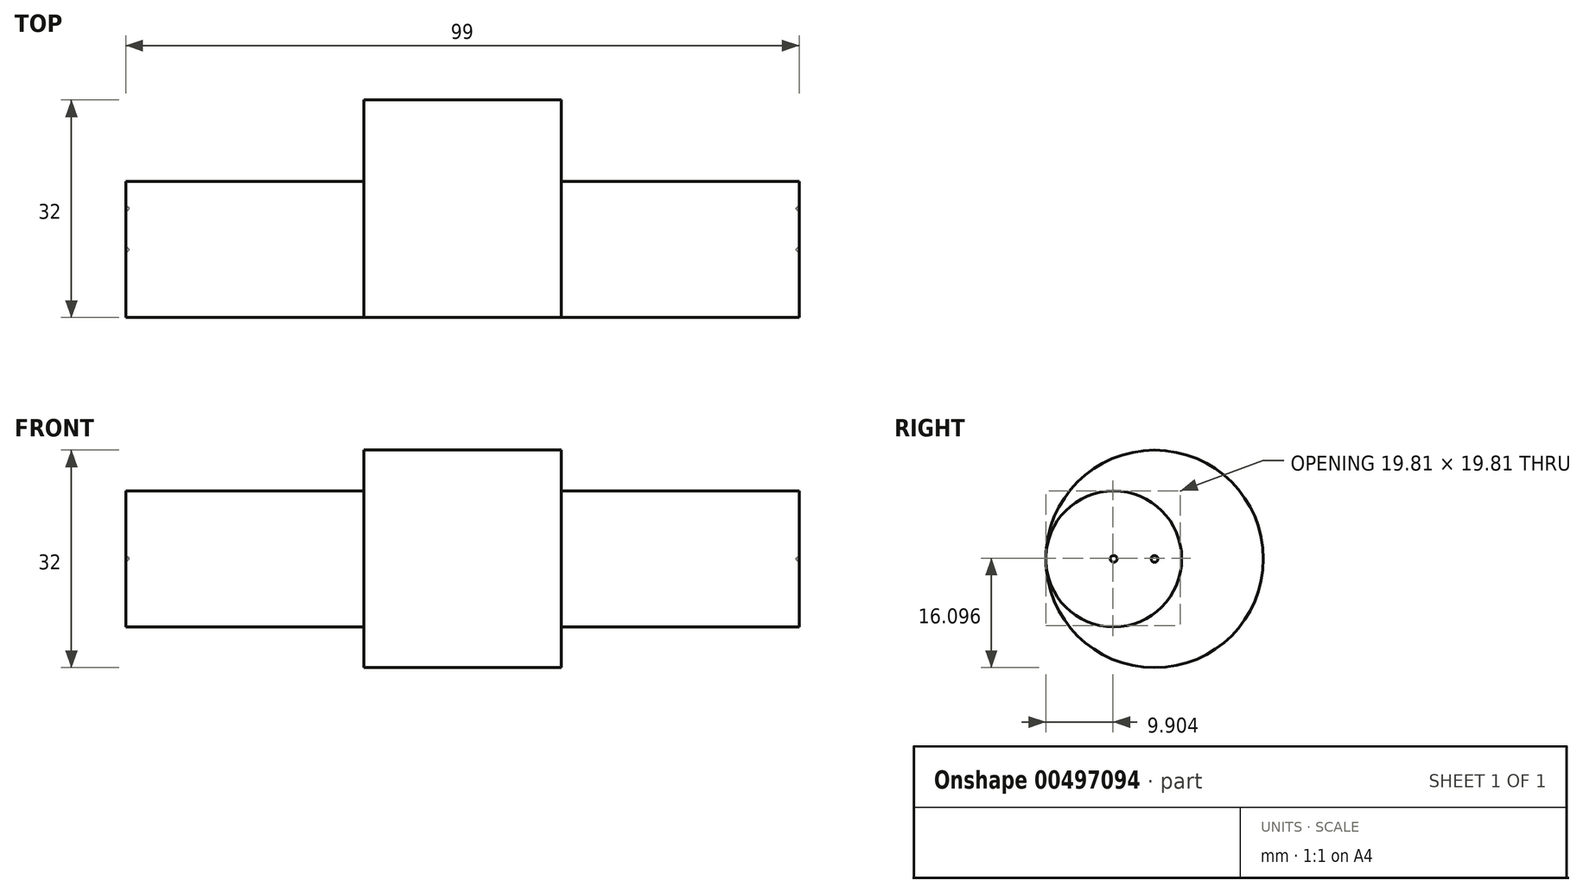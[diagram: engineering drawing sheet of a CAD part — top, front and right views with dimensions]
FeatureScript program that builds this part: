
annotation { "Feature Type Name" : "Feature", "Feature Type Description" : "" }
export const myFeature = defineFeature(function(context is Context, id is Id, definition is map)
    precondition{}
    {
        {
            var Q0;
            Q0=qCreatedBy(makeId("Top.planeOp"),FACE);
            var sketch = newSketch(context, id + "F0", { "sketchPlane" : qUnion([Q0])});
            skLineSegment(sketch, "E0.bottom", {"start": v(0, -6) * mm, "end": v(35, -6) * mm});
            skLineSegment(sketch, "E0.top", {"start": v(0, -16) * mm, "end": v(35, -16) * mm});
            skLineSegment(sketch, "E0.left", {"start": v(0, -6) * mm, "end": v(0, -16) * mm});
            skLineSegment(sketch, "E0.right", {"start": v(35, -6) * mm, "end": v(35, -16) * mm});
            skLineSegment(sketch, "E1.bottom", {"start": v(64, -6) * mm, "end": v(99, -6) * mm});
            skLineSegment(sketch, "E1.top", {"start": v(64, -16) * mm, "end": v(99, -16) * mm});
            skLineSegment(sketch, "E1.left", {"start": v(64, -6) * mm, "end": v(64, -16) * mm});
            skLineSegment(sketch, "E1.right", {"start": v(99, -6) * mm, "end": v(99, -16) * mm});
            skLineSegment(sketch, "E2.bottom", {"start": v(35, -16) * mm, "end": v(64, -16) * mm});
            skLineSegment(sketch, "E2.top", {"start": v(35, 0) * mm, "end": v(64, 0) * mm});
            skLineSegment(sketch, "E2.left", {"start": v(35, -16) * mm, "end": v(35, 0) * mm});
            skLineSegment(sketch, "E2.right", {"start": v(64, -16) * mm, "end": v(64, 0) * mm});
            skLineSegment(sketch, "E3", {"start": v(0, -6.5) * mm, "end": v(0.5, -6) * mm});
            skLineSegment(sketch, "E4", {"start": v(99, -6.5) * mm, "end": v(98.5, -6) * mm});
            skLineSegment(sketch, "E5", {"start": v(0, -0.5) * mm, "end": v(0.5, 0) * mm});
            skLineSegment(sketch, "E6", {"start": v(0.5, 0) * mm, "end": v(0, 0) * mm});
            skLineSegment(sketch, "E7", {"start": v(0, 0) * mm, "end": v(0, -0.5) * mm});
            skLineSegment(sketch, "E8", {"start": v(49.5, -26.95) * mm, "end": v(49.5, -45.33) * mm, "construction": true});
            skPoint(sketch, "E8.startSnap0", {"position": v(49.5, -16) * mm});
            skLineSegment(sketch, "E9.MirrorCS", {"start": v(99, -0.5) * mm, "end": v(98.5, 0) * mm});
            skLineSegment(sketch, "E10.MirrorCS", {"start": v(98.5, 0) * mm, "end": v(99, 0) * mm});
            skLineSegment(sketch, "E11.MirrorCS", {"start": v(99, 0) * mm, "end": v(99, -0.5) * mm});
            skSolve(sketch);
        }
        {
            var Q0;
            {var subQ3=sQuery(id+"F0.wireOp",EDGE,"E2.bottom");Q0=makeQuery(id+"F0.imprint","IMPRINT",FACE,{"disambiguationData":[TD([[makeQuery(id+"F0.imprint","IMPRINT",EDGE,{"derivedFrom":subQ3}),1.0]])]});}
            var Q1;
            Q1=sQuery(id+"F0.wireOp",EDGE,"E2.top");
            revolve(context, id + "F1", {"entities" : qUnion([Q0]), "axis" : qUnion([Q1]), "revolveType" : RevolveType.FULL});
        }
        {
            var Q0;
            {var subQ1=sQuery(id+"F0.wireOp",EDGE,"E0.top");Q0=makeQuery(id+"F0.imprint","IMPRINT",FACE,{"disambiguationData":[TD([[makeQuery(id+"F0.imprint","IMPRINT",EDGE,{"derivedFrom":subQ1}),1.0]])]});}
            var Q1;
            {var subQ3=sQuery(id+"F0.wireOp",EDGE,"E1.top");Q1=makeQuery(id+"F0.imprint","IMPRINT",FACE,{"disambiguationData":[TD([[makeQuery(id+"F0.imprint","IMPRINT",EDGE,{"derivedFrom":subQ3}),1.0]])]});}
            var Q2;
            Q2=sQuery(id+"F0.wireOp",EDGE,"E0.bottom");
            revolve(context, id + "F2", {"operationType" : NewBodyOperationType.ADD, "entities" : qUnion([Q0, Q1]), "axis" : qUnion([Q2]), "revolveType" : RevolveType.FULL});
        }
        {
            var Q0;
            Q0=makeQuery(id+"F0.imprint","IMPRINT",FACE,{"disambiguationData":[TD([[makeQuery(id+"F0.imprint","IMPRINT",EDGE,{"derivedFrom":sQuery(id+"F0.wireOp",EDGE,"E5")}),1.0]])]});
            var Q1;
            Q1=makeQuery(id+"F0.imprint","IMPRINT",FACE,{"disambiguationData":[TD([[makeQuery(id+"F0.imprint","IMPRINT",EDGE,{"derivedFrom":sQuery(id+"F0.wireOp",EDGE,"E9.MirrorCS")}),-1.0]])]});
            var Q2;
            Q2=sQuery(id+"F0.wireOp",EDGE,"E2.top");
            revolve(context, id + "F3", {"operationType" : NewBodyOperationType.REMOVE, "entities" : qUnion([Q0, Q1]), "axis" : qUnion([Q2]), "revolveType" : RevolveType.FULL, "oppositeDirection" : true});
        }
    });
